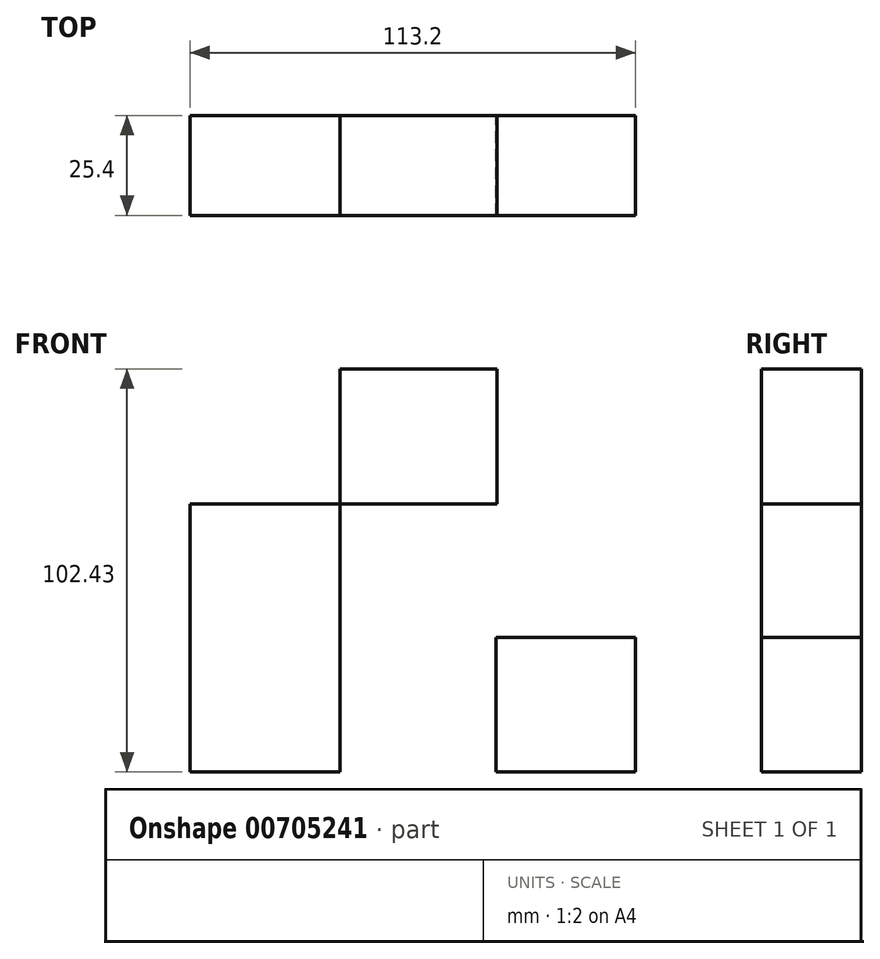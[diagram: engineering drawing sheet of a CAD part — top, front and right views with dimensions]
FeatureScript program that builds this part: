
annotation { "Feature Type Name" : "Feature", "Feature Type Description" : "" }
export const myFeature = defineFeature(function(context is Context, id is Id, definition is map)
    precondition{}
    {
        {
            var Q0;
            Q0=qCreatedBy(makeId("Front.planeOp"),FACE);
            var sketch = newSketch(context, id + "F0", { "sketchPlane" : qUnion([Q0])});
            skLineSegment(sketch, "E0.bottom", {"start": v(0, 0) * mm, "end": v(-38.16, 0) * mm});
            skLineSegment(sketch, "E0.top", {"start": v(0, 33.9) * mm, "end": v(-38.16, 33.9) * mm});
            skLineSegment(sketch, "E0.left", {"start": v(0, 0) * mm, "end": v(0, 33.9) * mm});
            skLineSegment(sketch, "E0.right", {"start": v(-38.16, 0) * mm, "end": v(-38.16, 33.9) * mm});
            skLineSegment(sketch, "E1.bottom", {"start": v(0, 33.9) * mm, "end": v(39.86, 33.9) * mm});
            skLineSegment(sketch, "E1.top", {"start": v(0, 68.24) * mm, "end": v(39.86, 68.24) * mm});
            skLineSegment(sketch, "E1.left", {"start": v(0, 33.9) * mm, "end": v(0, 68.24) * mm});
            skLineSegment(sketch, "E1.right", {"start": v(39.86, 33.9) * mm, "end": v(39.86, 68.24) * mm});
            skLineSegment(sketch, "E2.bottom", {"start": v(0, 33.9) * mm, "end": v(39.58, 33.9) * mm});
            skLineSegment(sketch, "E2.top", {"start": v(0, 0) * mm, "end": v(39.58, 0) * mm});
            skLineSegment(sketch, "E2.left", {"start": v(0, 33.9) * mm, "end": v(0, 0) * mm});
            skLineSegment(sketch, "E2.right", {"start": v(39.58, 33.9) * mm, "end": v(39.58, 0) * mm});
            skLineSegment(sketch, "E3.bottom", {"start": v(97.18, -56.89) * mm, "end": v(99.45, -56.89) * mm});
            skLineSegment(sketch, "E3.top", {"start": v(97.18, -54.33) * mm, "end": v(99.45, -54.33) * mm});
            skLineSegment(sketch, "E3.left", {"start": v(97.18, -56.89) * mm, "end": v(97.18, -54.33) * mm});
            skLineSegment(sketch, "E3.right", {"start": v(99.45, -56.89) * mm, "end": v(99.45, -54.33) * mm});
            skLineSegment(sketch, "E4.top", {"start": v(0, -34.19) * mm, "end": v(-38.16, -34.19) * mm});
            skLineSegment(sketch, "E4.left", {"start": v(0, 0) * mm, "end": v(0, -34.19) * mm});
            skLineSegment(sketch, "E4.right", {"start": v(-38.16, 0) * mm, "end": v(-38.16, -34.19) * mm});
            skLineSegment(sketch, "E5.bottom", {"start": v(39.58, 0) * mm, "end": v(0, 0) * mm});
            skLineSegment(sketch, "E5.top", {"start": v(39.58, -34.19) * mm, "end": v(0, -34.19) * mm});
            skLineSegment(sketch, "E5.left", {"start": v(39.58, 0) * mm, "end": v(39.58, -34.19) * mm});
            skLineSegment(sketch, "E6.bottom", {"start": v(39.58, 0) * mm, "end": v(75.04, 0) * mm});
            skLineSegment(sketch, "E6.top", {"start": v(39.58, -34.19) * mm, "end": v(75.04, -34.19) * mm});
            skLineSegment(sketch, "E6.right", {"start": v(75.04, 0) * mm, "end": v(75.04, -34.19) * mm});
            skSolve(sketch);
        }
        {
            var Q0;
            Q0=makeQuery(id+"F0.imprint","IMPRINT",FACE,{"disambiguationData":[TD([[makeQuery(id+"F0.imprint","IMPRINT",EDGE,{"derivedFrom":sQuery(id+"F0.wireOp",EDGE,"E0.top")}),1.0]])]});
            var Q1;
            Q1=makeQuery(id+"F0.imprint","IMPRINT",FACE,{"disambiguationData":[TD([[makeQuery(id+"F0.imprint","IMPRINT",EDGE,{"derivedFrom":sQuery(id+"F0.wireOp",EDGE,"E1.bottom")}),1.0]])]});
            var Q2;
            Q2=makeQuery(id+"F0.imprint","IMPRINT",FACE,{"disambiguationData":[TD([[makeQuery(id+"F0.imprint","IMPRINT",EDGE,{"derivedFrom":sQuery(id+"F0.wireOp",EDGE,"E2.bottom")}),-1.0]])]});
            var Q3;
            Q3=makeQuery(id+"F0.imprint","IMPRINT",FACE,{"disambiguationData":[TD([[makeQuery(id+"F0.imprint","IMPRINT",EDGE,{"derivedFrom":sQuery(id+"F0.wireOp",EDGE,"E0.bottom")}),1.0]])]});
            var Q4;
            Q4=makeQuery(id+"F0.imprint","IMPRINT",FACE,{"disambiguationData":[TD([[makeQuery(id+"F0.imprint","IMPRINT",EDGE,{"derivedFrom":sQuery(id+"F0.wireOp",EDGE,"E5.bottom")}),1.0]])]});
            var Q5;
            Q5=makeQuery(id+"F0.imprint","IMPRINT",FACE,{"disambiguationData":[TD([[makeQuery(id+"F0.imprint","IMPRINT",EDGE,{"derivedFrom":sQuery(id+"F0.wireOp",EDGE,"E6.bottom")}),-1.0]])]});
            extrude(context, id + "F1", {"entities" : qUnion([Q0, Q1, Q2, Q3, Q4, Q5]), "depth" : 25.4 * mm, "offsetDistance" : 25.4 * mm});
        }
    });
